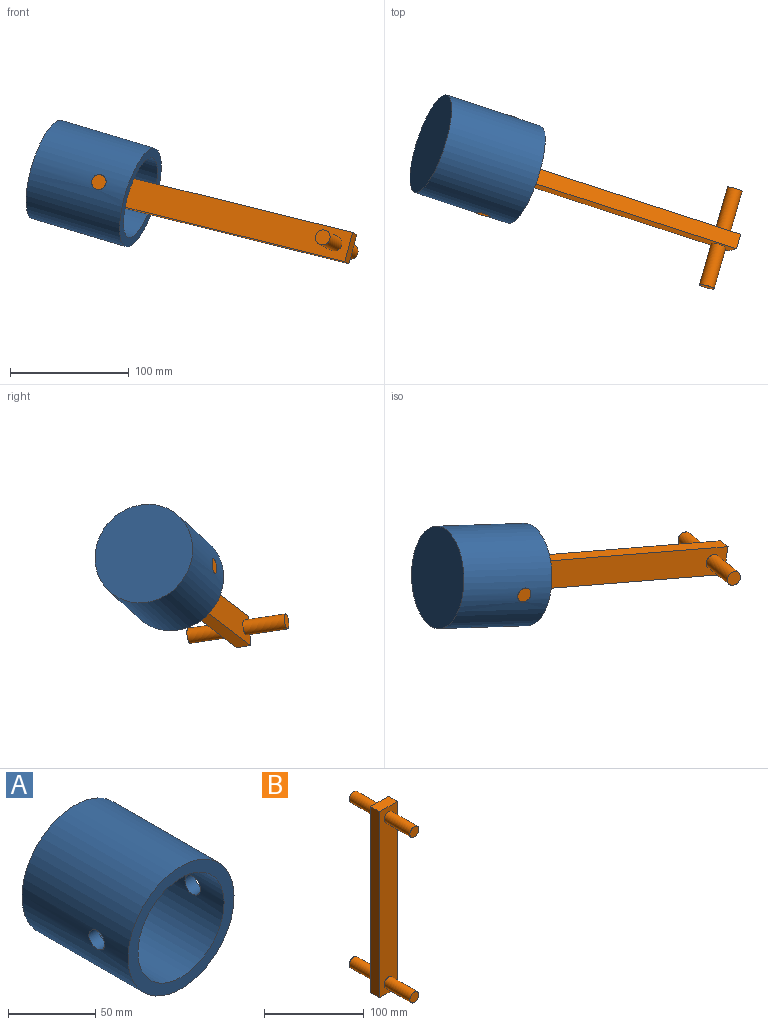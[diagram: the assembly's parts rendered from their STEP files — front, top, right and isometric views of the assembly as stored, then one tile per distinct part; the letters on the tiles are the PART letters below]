
ASSEMBLY  parts=2 mates=1
PART A: 7 faces, bbox 86.1x86.1x86.1 mm
  f0: cylinder r=43.05mm len=86.11mm, axis (0,1,0), area 23038.4mm2, adj f2,f3,f5,f6
  f1: cylinder r=34.98mm len=76.2mm, axis (0,-1,0), area 16492.9mm2, adj f2,f4,f5,f6
  f2: plane 86.11x86.11mm, normal (0,-1,0), area 1979.1mm2, adj f0,f1
  f3: plane 86.11x86.11mm, normal (0,1,0), area 5823.1mm2, adj f0
  f4: plane 69.96x69.96mm, normal (0,-1,0), area 3844mm2, adj f1
  f5: cylinder r=6.35mm len=12.7mm, axis (-1,0,0), area 324.3mm2, adj f0,f1
  f6: cylinder r=6.35mm len=12.7mm, axis (-1,0,0), area 324.3mm2, adj f0,f1
PART B: 14 faces, bbox 25.4x86.1x228.6 mm
  f0: plane 228.6x12.7mm, normal (1,0,0), area 2903.2mm2, adj f1,f3,f4,f5
  f1: plane 25.4x12.7mm, normal (0,0,1), area 322.6mm2, adj f0,f2,f4,f5
  f2: plane 228.6x12.7mm, normal (-1,0,0), area 2903.2mm2, adj f1,f3,f4,f5
  f3: plane 25.4x12.7mm, normal (0,0,-1), area 322.6mm2, adj f0,f2,f4,f5
  f4: plane 228.6x25.4mm, normal (0,1,0), area 5553.1mm2, adj f0,f1,f2,f3,f8,f12
  f5: plane 228.6x25.4mm, normal (0,-1,0), area 5553.1mm2, adj f0,f1,f2,f3,f7,f11
  f6: plane 12.7x12.7mm, normal (0,-1,0), area 126.7mm2, adj f7
  f7: cylinder r=6.35mm len=36.7mm, axis (0,-1,0), area 1464.4mm2, adj f5,f6
  f8: cylinder r=6.35mm len=36.7mm, axis (0,-1,0), area 1464.4mm2, adj f4,f9
  f9: plane 12.7x12.7mm, normal (0,1,0), area 126.7mm2, adj f8
  f10: plane 12.7x12.7mm, normal (0,-1,0), area 126.7mm2, adj f11
  f11: cylinder r=6.35mm len=36.7mm, axis (0,-1,0), area 1464.4mm2, adj f5,f10
  f12: cylinder r=6.35mm len=36.7mm, axis (0,-1,0), area 1464.4mm2, adj f4,f13
  f13: plane 12.7x12.7mm, normal (0,1,0), area 126.7mm2, adj f12
PLACE A rot(axis=(0.11,0.23,0.97),74.7deg) t=(-101.63,43.23,28.08)mm
PLACE B rot(axis=(0.79,-0.07,0.61),163.8deg) t=(49.7,0.58,-12.6)mm
MATE revolute B.f11 <-> A.f5  axis (0.27,0.95,-0.14) through (-34.4,65.92,5.51)mm
